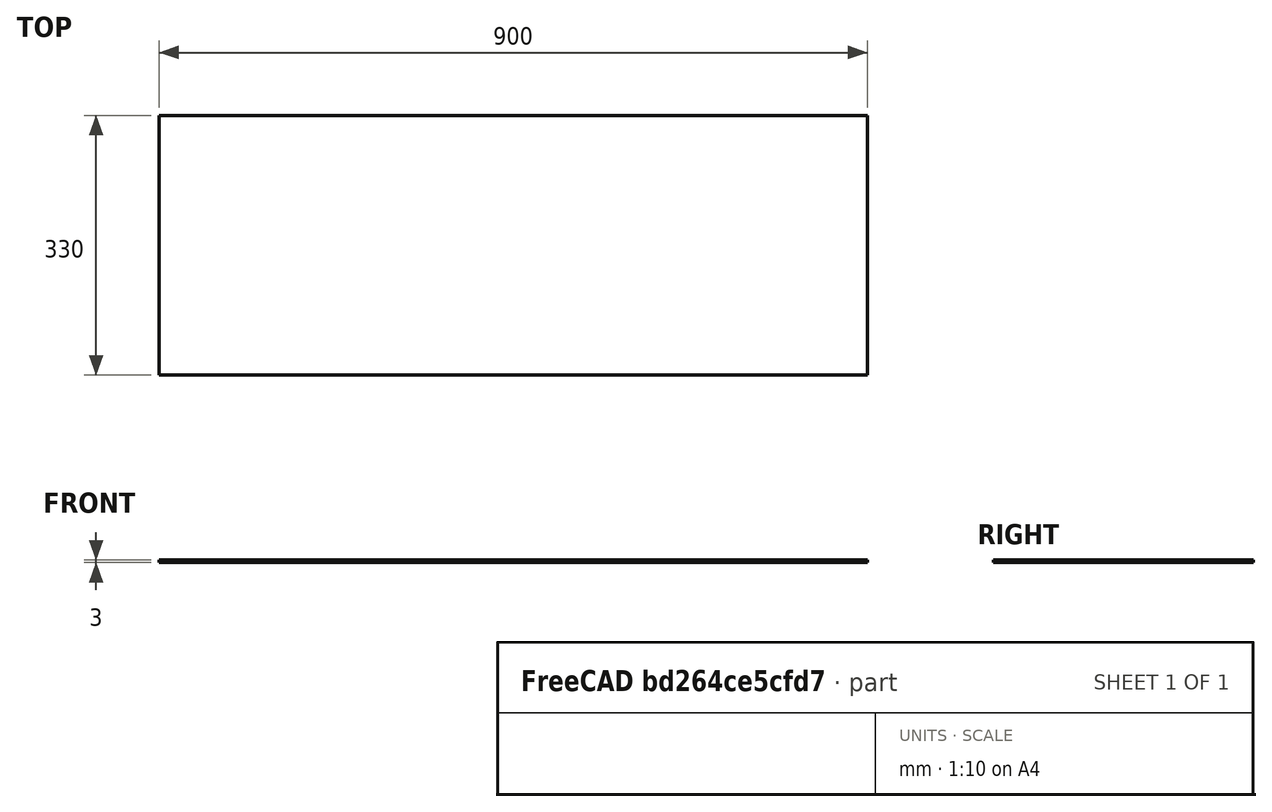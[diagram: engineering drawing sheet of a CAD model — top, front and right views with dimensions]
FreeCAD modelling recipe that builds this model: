
FCSTD DOCUMENT  (FreeCAD 0.16R6704 (Git))
Label: plaque_pmma
License: All rights reserved
LicenseURL: http://en.wikipedia.org/wiki/All_rights_reserved
objects: Sketcher::SketchObject×1, PartDesign::Pad×1
note: 3 computed .brp shape members not serialized (recipe doc carries the construction recipe); baked Part::Feature solids carry a one-line shape summary decoded from their .brp

FEATURE [Sketcher::SketchObject] Sketch001
  sketch-geometry (4):
    g0: LineSegment StartX=0 StartY=0 StartZ=0 EndX=900 EndY=0 EndZ=0
    g1: LineSegment StartX=900 StartY=0 StartZ=0 EndX=900 EndY=330 EndZ=0
    g2: LineSegment StartX=900 StartY=330 StartZ=0 EndX=0 EndY=330 EndZ=0
    g3: LineSegment StartX=0 StartY=330 StartZ=0 EndX=0 EndY=0 EndZ=0
  constraints (11):
    c: Coincident(g0,g1)
    c: Coincident(g1,g2)
    c: Coincident(g2,g3)
    c: Coincident(g3,g0)
    c: Horizontal(g0)
    c: Horizontal(g2)
    c: Vertical(g1)
    c: Vertical(g3)
    c: Coincident(g0,g-1)
    c: DistanceX(g0,g0) = 900
    c: DistanceY(g3,g3) = 330
FEATURE [PartDesign::Pad] Pad
  Length = 3
  Length2 = 100
  Sketch = -> Sketch001
  Type = 0
